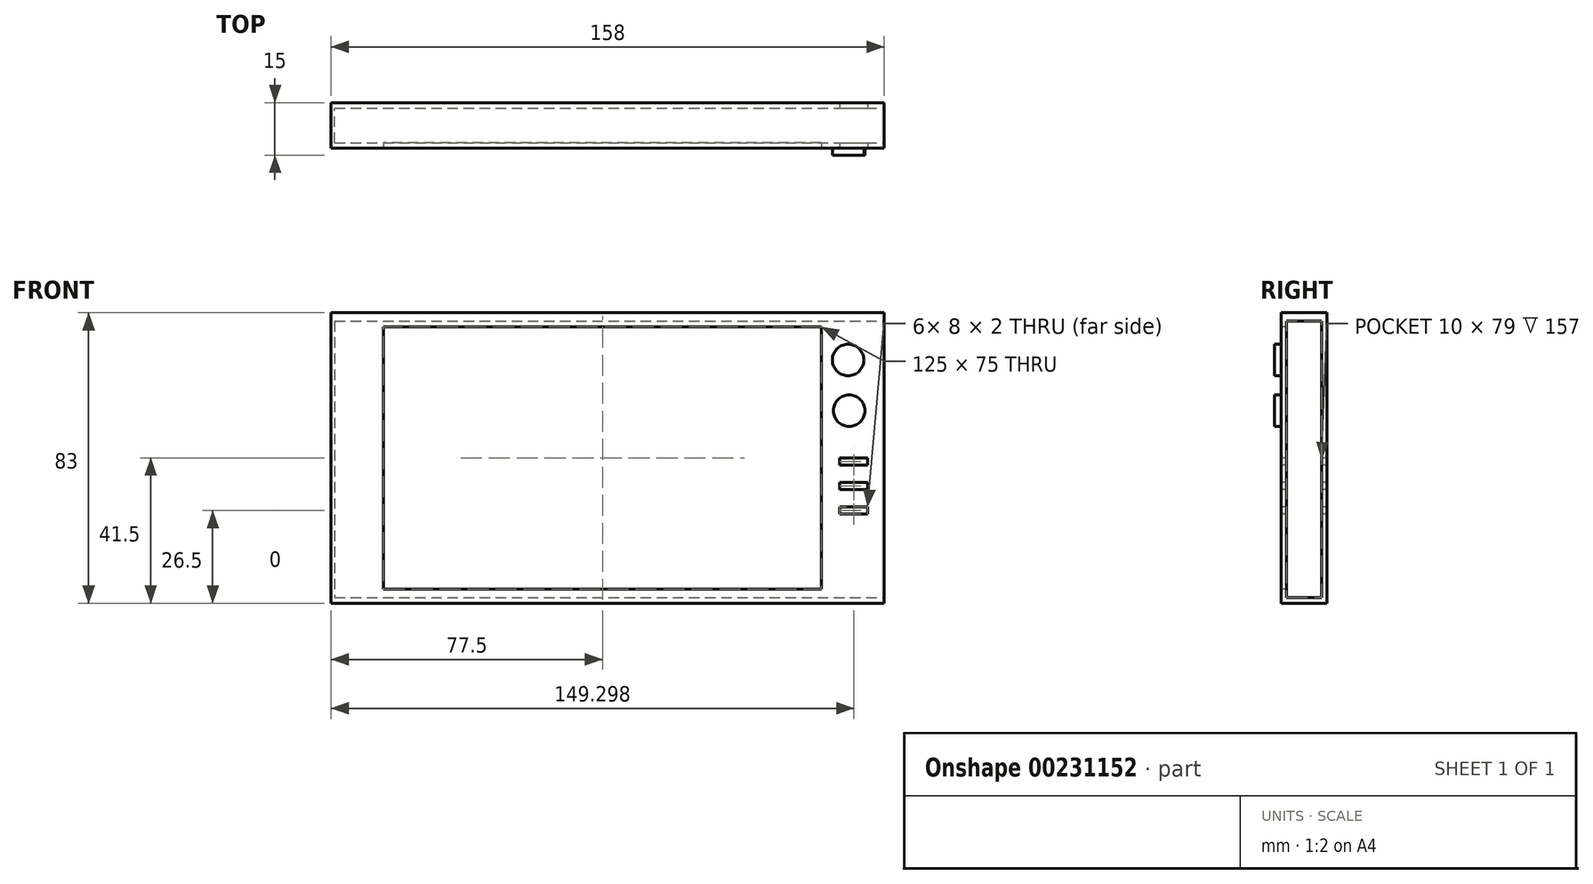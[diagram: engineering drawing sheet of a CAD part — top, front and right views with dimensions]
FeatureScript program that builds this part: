
annotation { "Feature Type Name" : "Feature", "Feature Type Description" : "" }
export const myFeature = defineFeature(function(context is Context, id is Id, definition is map)
    precondition{}
    {
        {
            var Q0;
            Q0=qCreatedBy(makeId("Front.planeOp"),FACE);
            var sketch = newSketch(context, id + "F0", { "sketchPlane" : qUnion([Q0])});
            skLineSegment(sketch, "E0.bottom", {"start": v(0, 0) * mm, "end": v(158, 0) * mm});
            skLineSegment(sketch, "E0.top", {"start": v(0, 83) * mm, "end": v(158, 83) * mm});
            skLineSegment(sketch, "E0.left", {"start": v(0, 0) * mm, "end": v(0, 83) * mm});
            skLineSegment(sketch, "E0.right", {"start": v(158, 0) * mm, "end": v(158, 83) * mm});
            skSolve(sketch);
        }
        {
            var Q0;
            Q0 = qSketchRegion(id + "F0", true);
            extrude(context, id + "F1", {"entities" : qUnion([Q0]), "depth" : 13 * mm});
        }
        {
            var Q0;
            Q0=makeQuery(id+"F1.opExtrude","CAP_FACE",FACE,{"disambiguationData":[OSD([sQuery(id+"F0.wireOp",EDGE,"E0.bottom"),sQuery(id+"F0.wireOp",EDGE,"E0.top"),sQuery(id+"F0.wireOp",EDGE,"E0.left"),sQuery(id+"F0.wireOp",EDGE,"E0.right")])],"isStart":false});
            var sketch = newSketch(context, id + "F2", { "sketchPlane" : qUnion([Q0])});
            skLineSegment(sketch, "E1.bottom", {"start": v(15, 79) * mm, "end": v(140, 79) * mm});
            skLineSegment(sketch, "E1.top", {"start": v(15, 4) * mm, "end": v(140, 4) * mm});
            skLineSegment(sketch, "E1.left", {"start": v(15, 79) * mm, "end": v(15, 4) * mm});
            skLineSegment(sketch, "E1.right", {"start": v(140, 79) * mm, "end": v(140, 4) * mm});
            skCircle(sketch, "E2", {"center": v(148.26, 70.16) * mm, "radius": 4 * mm});
            skCircle(sketch, "E3", {"center": v(148.26, 56.22) * mm, "radius": 4 * mm});
            skSolve(sketch);
        }
        {
            var Q0;
            Q0=makeQuery(id+"F2.imprint","IMPRINT",FACE,{"disambiguationData":[TD([[makeQuery(id+"F2.imprint","IMPRINT",EDGE,{"derivedFrom":sQuery(id+"F2.wireOp",EDGE,"E1.bottom")}),-1.0]])]});
            extrude(context, id + "F3", {"entities" : qUnion([Q0]), "operationType" : NewBodyOperationType.REMOVE, "oppositeDirection" : true, "depth" : 10 * mm});
        }
        {
            var Q0;
            Q0=makeQuery(id+"F1.opExtrude","SWEPT_FACE",FACE,{"disambiguationData":[OSD([sQuery(id+"F0.wireOp",EDGE,"E0.right")])]});
            var sketch = newSketch(context, id + "F4", { "sketchPlane" : qUnion([Q0])});
            skLineSegment(sketch, "E4.bottom", {"start": v(-11.5, 80.58) * mm, "end": v(-1.5, 80.58) * mm});
            skLineSegment(sketch, "E4.top", {"start": v(-11.5, 1.58) * mm, "end": v(-1.5, 1.58) * mm});
            skLineSegment(sketch, "E4.left", {"start": v(-11.5, 80.58) * mm, "end": v(-11.5, 1.58) * mm});
            skLineSegment(sketch, "E4.right", {"start": v(-1.5, 80.58) * mm, "end": v(-1.5, 1.58) * mm});
            skSolve(sketch);
        }
        {
            var Q0;
            Q0 = qSketchRegion(id + "F4", true);
            extrude(context, id + "F5", {"entities" : qUnion([Q0]), "operationType" : NewBodyOperationType.REMOVE, "oppositeDirection" : true, "depth" : 157 * mm});
        }
        {
            var Q0;
            Q0=makeQuery(id+"F1.opExtrude","CAP_FACE",FACE,{"disambiguationData":[OSD([sQuery(id+"F0.wireOp",EDGE,"E0.bottom"),sQuery(id+"F0.wireOp",EDGE,"E0.top"),sQuery(id+"F0.wireOp",EDGE,"E0.left"),sQuery(id+"F0.wireOp",EDGE,"E0.right")])],"isStart":false});
            var sketch = newSketch(context, id + "F6", { "sketchPlane" : qUnion([Q0])});
            skCircle(sketch, "E5", {"center": v(147.66, 69.5) * mm, "radius": 4.5 * mm});
            skSolve(sketch);
        }
        {
            var Q0;
            Q0 = qSketchRegion(id + "F6", true);
            extrude(context, id + "F7", {"entities" : qUnion([Q0]), "operationType" : NewBodyOperationType.ADD, "depth" : 2 * mm});
        }
        {
            var Q0;
            Q0=makeQuery(id+"F1.opExtrude","CAP_FACE",FACE,{"disambiguationData":[OSD([sQuery(id+"F0.wireOp",EDGE,"E0.bottom"),sQuery(id+"F0.wireOp",EDGE,"E0.top"),sQuery(id+"F0.wireOp",EDGE,"E0.left"),sQuery(id+"F0.wireOp",EDGE,"E0.right")])],"isStart":false});
            var sketch = newSketch(context, id + "F8", { "sketchPlane" : qUnion([Q0])});
            skCircle(sketch, "E6", {"center": v(147.96, 55.01) * mm, "radius": 4.5 * mm});
            skSolve(sketch);
        }
        {
            var Q0;
            Q0 = qSketchRegion(id + "F8", true);
            extrude(context, id + "F9", {"entities" : qUnion([Q0]), "operationType" : NewBodyOperationType.ADD, "depth" : 2 * mm});
        }
        {
            var Q0;
            Q0=makeQuery(id+"F1.opExtrude","CAP_FACE",FACE,{"disambiguationData":[OSD([sQuery(id+"F0.wireOp",EDGE,"E0.bottom"),sQuery(id+"F0.wireOp",EDGE,"E0.top"),sQuery(id+"F0.wireOp",EDGE,"E0.left"),sQuery(id+"F0.wireOp",EDGE,"E0.right")])],"isStart":false});
            var sketch = newSketch(context, id + "F10", { "sketchPlane" : qUnion([Q0])});
            skPoint(sketch, "E7.firstSnap0", {"position": v(140, 41.5) * mm});
            skLineSegment(sketch, "E7.bottom", {"start": v(145.3, 41.5) * mm, "end": v(153.3, 41.5) * mm});
            skLineSegment(sketch, "E7.top", {"start": v(145.3, 39.5) * mm, "end": v(153.3, 39.5) * mm});
            skLineSegment(sketch, "E7.left", {"start": v(145.3, 41.5) * mm, "end": v(145.3, 39.5) * mm});
            skLineSegment(sketch, "E7.right", {"start": v(153.3, 41.5) * mm, "end": v(153.3, 39.5) * mm});
            skLineSegment(sketch, "E8.bottom", {"start": v(145.3, 34.5) * mm, "end": v(153.3, 34.5) * mm});
            skLineSegment(sketch, "E8.top", {"start": v(145.3, 32.5) * mm, "end": v(153.3, 32.5) * mm});
            skLineSegment(sketch, "E8.left", {"start": v(145.3, 34.5) * mm, "end": v(145.3, 32.5) * mm});
            skLineSegment(sketch, "E8.right", {"start": v(153.3, 34.5) * mm, "end": v(153.3, 32.5) * mm});
            skLineSegment(sketch, "E9.bottom", {"start": v(145.3, 27.5) * mm, "end": v(153.3, 27.5) * mm});
            skLineSegment(sketch, "E9.top", {"start": v(145.3, 25.5) * mm, "end": v(153.3, 25.5) * mm});
            skLineSegment(sketch, "E9.left", {"start": v(145.3, 27.5) * mm, "end": v(145.3, 25.5) * mm});
            skLineSegment(sketch, "E9.right", {"start": v(153.3, 27.5) * mm, "end": v(153.3, 25.5) * mm});
            skSolve(sketch);
        }
        {
            var Q0;
            Q0 = qSketchRegion(id + "F10", true);
            extrude(context, id + "F11", {"entities" : qUnion([Q0]), "operationType" : NewBodyOperationType.REMOVE, "oppositeDirection" : true, "depth" : 25 * mm});
        }
    });
